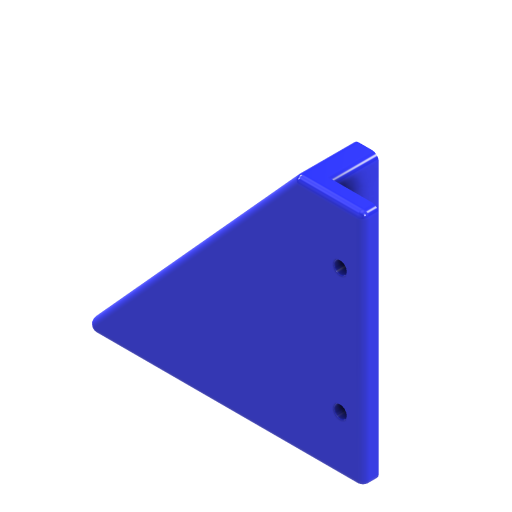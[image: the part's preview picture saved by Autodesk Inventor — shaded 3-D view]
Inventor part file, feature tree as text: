
AUTODESK INVENTOR PART (.ipt)
format: ipt  version: 2024.1 (Build 281209000, 209)  size: 164,352 bytes
history: native  units: mm
features: sketch x4, extrude x2, hole x2, projected_geometry x2, fillet x1
ambient origin geometry x8: Origin, YZ Plane, XZ Plane, XY Plane, X Axis, Y Axis, Z Axis, Center Point
bodies: Solid1 (feature_tree)
feature tree (11):
  extrude  "Extrusion1"  Depth=125.0mm
  extrude  "Extrusion2"  Depth=7.0mm TaperAngle=0.0deg
  fillet  "Fillet1"  Radius=20.0mm
  hole  "Hole1"  [1 undecoded]
  hole  "Hole3"  [1 undecoded]
  sketch  "Sketch1"  dims[d0=105.0mm d1=125.0mm]
  sketch  "Sketch2"  dims[d3=30.0mm d4=7.0mm d5=0.0mm d6=20.0mm]
  projected_geometry  "Projected Loop1"
  sketch  "Sketch3"  dims[d7=5.0mm d8=20.0mm d9=0.0mm]
  sketch  "Sketch5"  dims[d10=3.0mm d11=5.8mm d12=6.0mm d13=10.4mm d14=2.0mm d15=90.0deg d16=8.0mm d17=20.594885mm d18=25.0mm d19=10.0mm d23=55.0mm d31=5.8mm d32=6.0mm d33=4.0mm d34=2.0mm d35=90.0deg d36=8.0mm d37=20.594885mm d38=65.0mm d40=10.0mm]
  projected_geometry  "Projected Loop2"
note: 2 required parameter values undecoded (feature->parameter linkage not recoverable at this tier; creation-order binding heuristic only, values carry confidence <= 0.55)
